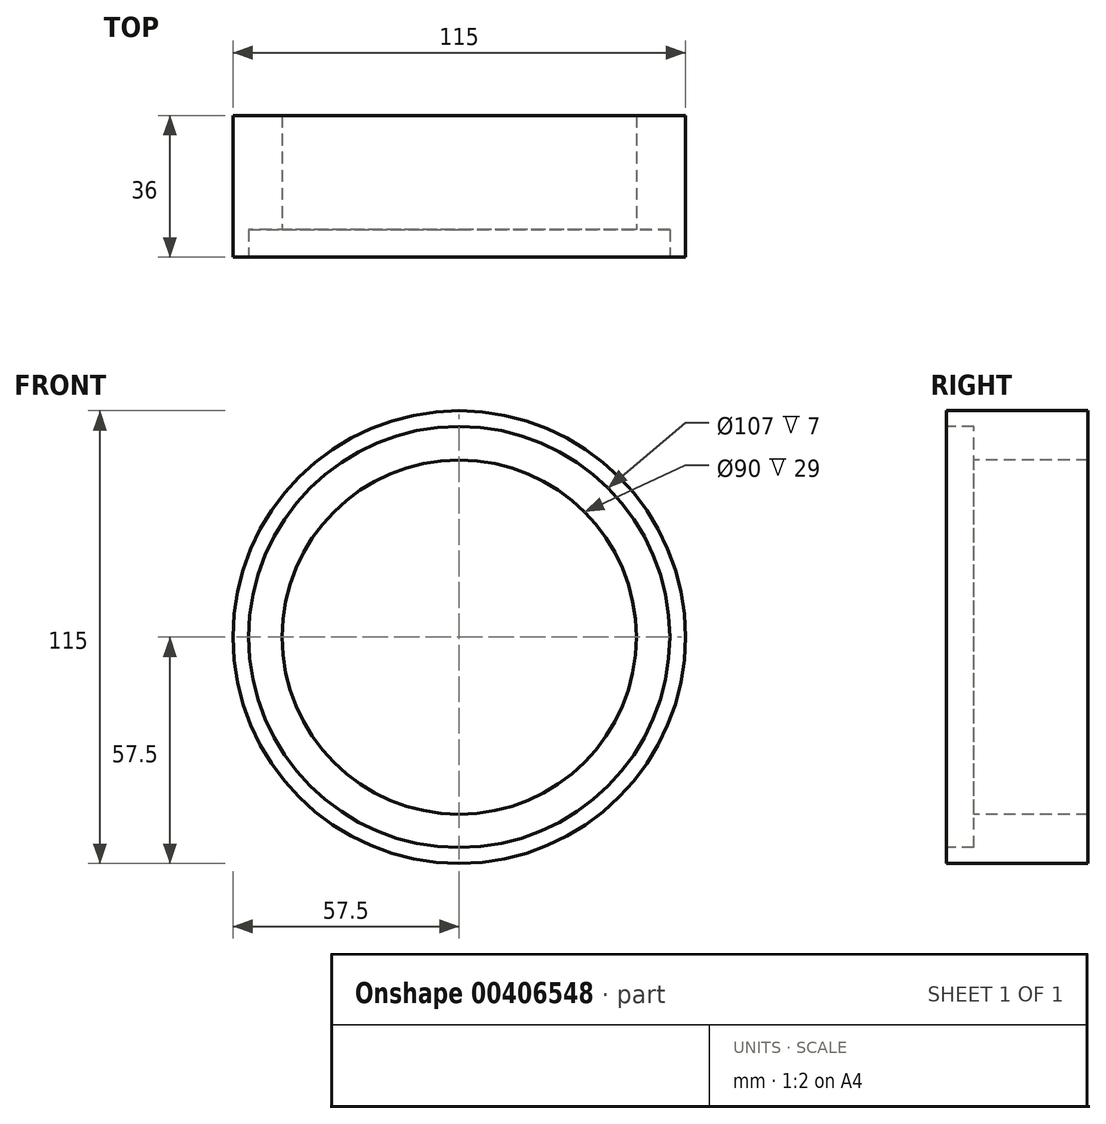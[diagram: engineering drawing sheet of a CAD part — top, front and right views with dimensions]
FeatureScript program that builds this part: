
annotation { "Feature Type Name" : "Feature", "Feature Type Description" : "" }
export const myFeature = defineFeature(function(context is Context, id is Id, definition is map)
    precondition{}
    {
        {
            var Q0;
            Q0=qCreatedBy(makeId("Front.planeOp"),FACE);
            var sketch = newSketch(context, id + "F0", { "sketchPlane" : qUnion([Q0])});
            skCircle(sketch, "E0", {"center": v(0, 0) * mm, "radius": 57.5 * mm});
            skSolve(sketch);
        }
        {
            var Q0;
            Q0=makeQuery(id+"F0.imprint","IMPRINT",FACE,{"disambiguationData":[TD([[makeQuery(id+"F0.imprint","IMPRINT",EDGE,{"derivedFrom":sQuery(id+"F0.wireOp",EDGE,"E0")}),1.0]])]});
            extrude(context, id + "F1", {"entities" : qUnion([Q0]), "depth" : 36 * mm});
        }
        {
            var Q0;
            Q0=makeQuery(id+"F1.opExtrude","CAP_FACE",FACE,{"disambiguationData":[OSD([sQuery(id+"F0.wireOp",EDGE,"E0")])],"isStart":false});
            var sketch = newSketch(context, id + "F2", { "sketchPlane" : qUnion([Q0])});
            skCircle(sketch, "E1", {"center": v(0, 0) * mm, "radius": 53.5 * mm});
            skSolve(sketch);
        }
        {
            var Q0;
            Q0=makeQuery(id+"F2.imprint","IMPRINT",FACE,{"disambiguationData":[TD([[makeQuery(id+"F2.imprint","IMPRINT",EDGE,{"derivedFrom":sQuery(id+"F2.wireOp",EDGE,"E1")}),1.0]])]});
            extrude(context, id + "F3", {"entities" : qUnion([Q0]), "operationType" : NewBodyOperationType.REMOVE, "oppositeDirection" : true, "depth" : 7 * mm});
        }
        {
            var Q0;
            Q0=makeQuery(id+"F3.boolean.opBoolean","COPY",FACE,{"derivedFrom":makeQuery(id+"F3.opExtrude","CAP_FACE",FACE,{"disambiguationData":[OSD([sQuery(id+"F2.wireOp",EDGE,"E1")])],"isStart":false})});
            var sketch = newSketch(context, id + "F4", { "sketchPlane" : qUnion([Q0])});
            skCircle(sketch, "E2", {"center": v(0, 0) * mm, "radius": 45 * mm});
            skSolve(sketch);
        }
        {
            var Q0;
            Q0=makeQuery(id+"F4.imprint","IMPRINT",FACE,{"disambiguationData":[TD([[makeQuery(id+"F4.imprint","IMPRINT",EDGE,{"derivedFrom":sQuery(id+"F4.wireOp",EDGE,"E2")}),1.0]])]});
            extrude(context, id + "F5", {"entities" : qUnion([Q0]), "operationType" : NewBodyOperationType.REMOVE, "endBound" : BoundingType.THROUGH_ALL, "oppositeDirection" : true, "depth" : 25 * mm});
        }
    });
